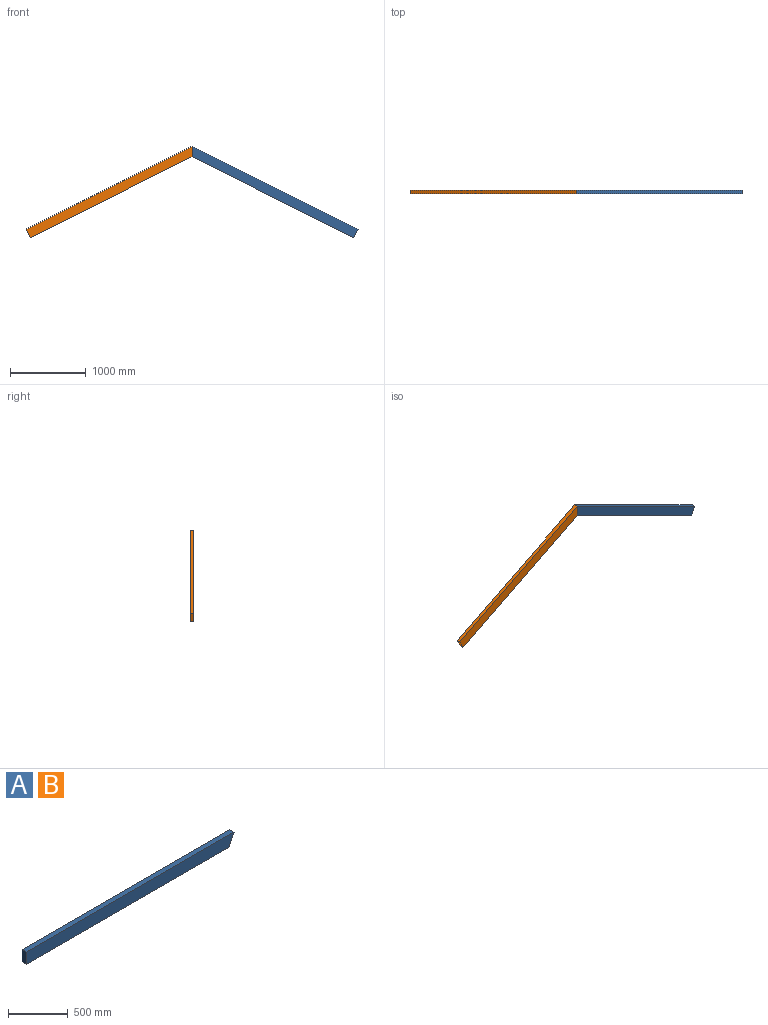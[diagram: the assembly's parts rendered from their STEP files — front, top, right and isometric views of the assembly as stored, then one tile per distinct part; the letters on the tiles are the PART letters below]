
ASSEMBLY  parts=2 mates=1
PART A: 6 faces, bbox 2450x50x125 mm
  f0: plane 2387.5x50mm, normal (0,0,-1), area 119375mm2, adj f1,f3,f4,f5
  f1: plane 2450x125mm, normal (0,1,0), area 302343.7mm2, adj f0,f2,f4,f5
  f2: plane 2450x50mm, normal (0,0,1), area 122500mm2, adj f1,f3,f4,f5
  f3: plane 2450x125mm, normal (0,-1,0), area 302343.7mm2, adj f0,f2,f4,f5
  f4: plane 125x50mm, normal (-1,0,0), area 6250mm2, adj f0,f1,f2,f3
  f5: plane 125x62.5mm, normal (0.89,0,-0.45), area 6987.7mm2, adj f0,f1,f2,f3
PART B: same geometry as A
PLACE A rot(axis=(-0.23,0,-0.97),180deg) t=(-27.95,0,13.98)mm
PLACE B rot(axis=(0,-1,0),26.6deg) t=(27.95,0,13.98)mm
MATE fastened A.f5 <-> B.f5  axis (-1,0,0) through (0,0,0)mm
